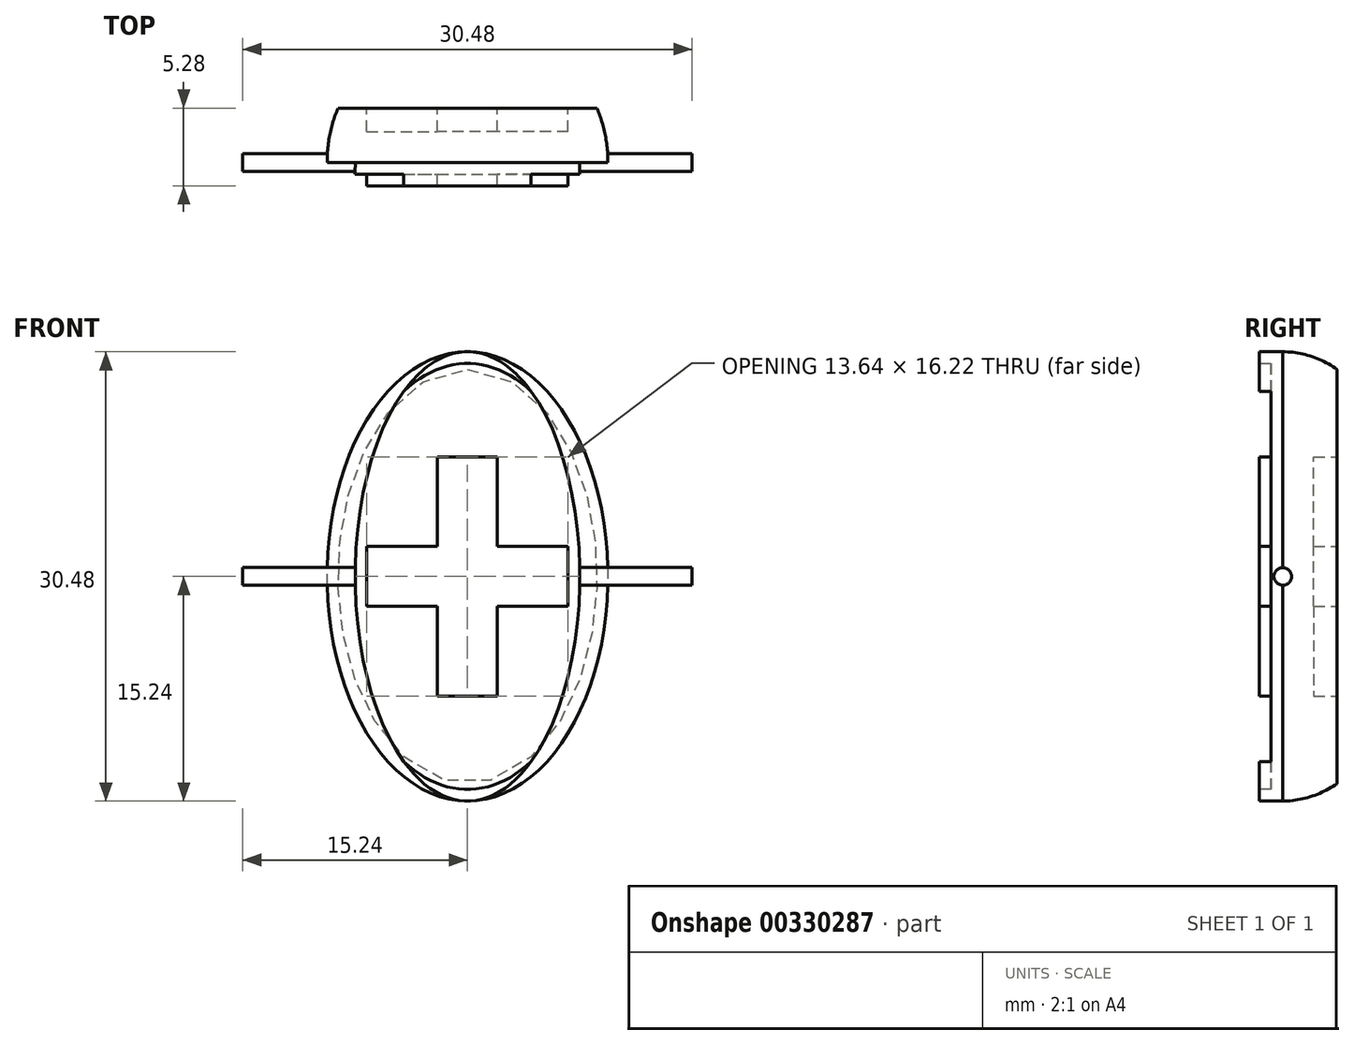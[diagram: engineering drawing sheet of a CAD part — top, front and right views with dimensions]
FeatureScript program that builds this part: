
annotation { "Feature Type Name" : "Feature", "Feature Type Description" : "" }
export const myFeature = defineFeature(function(context is Context, id is Id, definition is map)
    precondition{}
    {
        {
            var Q0;
            Q0=qCreatedBy(makeId("Front.planeOp"),FACE);
            var sketch = newSketch(context, id + "F0", { "sketchPlane" : qUnion([Q0])});
            skEllipticalArc(sketch, "E0", {});
            skLineSegment(sketch, "E1", {"start": v(0, 15.24) * mm, "end": v(0, -15.24) * mm});
            const initialGuessF0  = {"E0": [0, 0, 0, 1, 0.01524, 0.009525, 3.141592653589793, 0]};
            skSetInitialGuess(sketch, initialGuessF0);
            skSolve(sketch);
        }
        {
            var Q0;
            Q0=qSketchRegion(id+"F0",true);
            var Q1;
            Q1=sQuery(id+"F0.wireOp",EDGE,"E1");
            revolve(context, id + "F1", {"entities" : qUnion([Q0]), "axis" : qUnion([Q1]), "revolveType" : RevolveType.ONE_DIRECTION, "oppositeDirection" : true, "angle" : 180 * degree});
        }
        {
            var Q0;
            Q0=qCreatedBy(makeId("Right.planeOp"),FACE);
            var sketch = newSketch(context, id + "F2", { "sketchPlane" : qUnion([Q0])});
            skLineSegment(sketch, "E2.bottom", {"start": v(3.69, 15.9) * mm, "end": v(30.72, 15.9) * mm});
            skLineSegment(sketch, "E2.top", {"start": v(3.69, -22.6) * mm, "end": v(30.72, -22.6) * mm});
            skLineSegment(sketch, "E2.left", {"start": v(3.69, 15.9) * mm, "end": v(3.69, -22.6) * mm});
            skLineSegment(sketch, "E2.right", {"start": v(30.72, 15.9) * mm, "end": v(30.72, -22.6) * mm});
            skSolve(sketch);
        }
        {
            var Q0;
            Q0=qSketchRegion(id+"F2",true);
            extrude(context, id + "F3", {"entities" : qUnion([Q0]), "operationType" : NewBodyOperationType.REMOVE, "oppositeDirection" : true, "depth" : 25.4 * mm, "symmetric" : true});
        }
        {
            var Q0;
            Q0=qCreatedBy(makeId("Right.planeOp"),FACE);
            var sketch = newSketch(context, id + "F4", { "sketchPlane" : qUnion([Q0])});
            skCircle(sketch, "E3", {"center": v(0, 0) * mm, "radius": 0.6 * mm});
            skSolve(sketch);
        }
        {
            var Q0;
            Q0=makeQuery(id+"F1.opRevolve","CAP_FACE",FACE,{"disambiguationData":[OSD([sQuery(id+"F0.wireOp",EDGE,"E0"),sQuery(id+"F0.wireOp",EDGE,"E1")])],"isStart":false});
            var sketch = newSketch(context, id + "F5", { "sketchPlane" : qUnion([Q0])});
            skEllipticalArc(sketch, "E4.0", {});
            skEllipticalArc(sketch, "E4.1", {});
            const initialGuessF5  = {"E4.0": [0, 0, 0, 1, 0.01524, 0.00762, 0, 3.141592653589793], "E4.1": [0, 0, 0, 1, 0.01524, 0.00762, 3.141592653589793, 0]};
            skSetInitialGuess(sketch, initialGuessF5);
            skSolve(sketch);
        }
        {
            var Q0;
            Q0=qSketchRegion(id+"F5",true);
            extrude(context, id + "F6", {"entities" : qUnion([Q0]), "operationType" : NewBodyOperationType.ADD, "depth" : 1.59 * mm});
        }
        {
            var Q0;
            Q0=qSketchRegion(id+"F4",true);
            extrude(context, id + "F7", {"entities" : qUnion([Q0]), "operationType" : NewBodyOperationType.ADD, "depth" : 30.48 * mm, "symmetric" : true});
        }
        {
            var Q0;
            Q0=makeQuery(id+"F6.opExtrude","CAP_FACE",FACE,{"disambiguationData":[OSD([sQuery(id+"F5.wireOp",EDGE,"E4.0"),sQuery(id+"F5.wireOp",EDGE,"E4.1")])],"isStart":false});
            var sketch = newSketch(context, id + "F8", { "sketchPlane" : qUnion([Q0])});
            skEllipse(sketch, "E5", {"center": v(0, 0) * mm, "majorRadius": 14.45 * mm, "minorRadius": 8.73 * mm, "majorAxis": v(0, 1)});
            skSolve(sketch);
        }
        {
            var Q0;
            Q0=qSketchRegion(id+"F8",true);
            extrude(context, id + "F9", {"entities" : qUnion([Q0]), "operationType" : NewBodyOperationType.REMOVE, "oppositeDirection" : true, "depth" : 0.8 * mm});
        }
        {
            var Q0;
            Q0=makeQuery(id+"F9.boolean.opBoolean","COPY",FACE,{"derivedFrom":makeQuery(id+"F9.opExtrude","CAP_FACE",FACE,{"disambiguationData":[OSD([sQuery(id+"F8.wireOp",EDGE,"E5")])],"isStart":false})});
            var sketch = newSketch(context, id + "F10", { "sketchPlane" : qUnion([Q0])});
            skSolve(sketch);
        }
        {
            var Q0;
            Q0=makeQuery(id+"F10.imprint","IMPRINT",FACE,{"disambiguationData":[TD([[makeQuery(id+"F10.imprint","IMPRINT",EDGE,{"derivedFrom":makeQuery(id+"F9.boolean.opBoolean","COPY",EDGE,{"derivedFrom":makeQuery(id+"F9.opExtrude","CAP_EDGE",EDGE,{"disambiguationData":[OSD([sQuery(id+"F8.wireOp",EDGE,"E5")])],"isStart":false})})}),1.0]])]});
            var sketch = newSketch(context, id + "F11", { "sketchPlane" : qUnion([Q0])});
            skLineSegment(sketch, "E6", {"start": v(0, 8.11) * mm, "end": v(-2.03, 8.11) * mm});
            skLineSegment(sketch, "E7", {"start": v(-6.82, 0) * mm, "end": v(-6.82, 2.03) * mm});
            skLineSegment(sketch, "E8", {"start": v(-6.82, 2.03) * mm, "end": v(-2.03, 2.03) * mm});
            skLineSegment(sketch, "E9", {"start": v(-2.03, 2.03) * mm, "end": v(-2.03, 8.11) * mm});
            skLineSegment(sketch, "E10.MirrorCS", {"start": v(-6.82, 0) * mm, "end": v(-6.82, -2.03) * mm});
            skLineSegment(sketch, "E11.MirrorCS", {"start": v(-2.03, -2.03) * mm, "end": v(-2.03, -8.11) * mm});
            skLineSegment(sketch, "E12.MirrorCS", {"start": v(0, -8.11) * mm, "end": v(-2.03, -8.11) * mm});
            skLineSegment(sketch, "E13.MirrorCS", {"start": v(-6.82, -2.03) * mm, "end": v(-2.03, -2.03) * mm});
            skLineSegment(sketch, "E14.MirrorCS", {"start": v(2.03, -2.03) * mm, "end": v(2.03, -8.11) * mm});
            skLineSegment(sketch, "E15.MirrorCS", {"start": v(2.03, 2.03) * mm, "end": v(2.03, 8.11) * mm});
            skLineSegment(sketch, "E16.MirrorCS", {"start": v(6.82, 0) * mm, "end": v(6.82, -2.03) * mm});
            skLineSegment(sketch, "E17.MirrorCS", {"start": v(0, 8.11) * mm, "end": v(2.03, 8.11) * mm});
            skLineSegment(sketch, "E18.MirrorCS", {"start": v(6.82, 0) * mm, "end": v(6.82, 2.03) * mm});
            skLineSegment(sketch, "E19.MirrorCS", {"start": v(6.82, 2.03) * mm, "end": v(2.03, 2.03) * mm});
            skLineSegment(sketch, "E20.MirrorCS", {"start": v(6.82, -2.03) * mm, "end": v(2.03, -2.03) * mm});
            skLineSegment(sketch, "E21.MirrorCS", {"start": v(0, -8.11) * mm, "end": v(2.03, -8.11) * mm});
            skSolve(sketch);
        }
        {
            var Q0;
            Q0=qSketchRegion(id+"F11",true);
            extrude(context, id + "F12", {"entities" : qUnion([Q0]), "operationType" : NewBodyOperationType.ADD, "depth" : 0.8 * mm});
        }
        {
            var Q0;
            Q0=makeQuery(id+"F3.boolean.opBoolean","COPY",FACE,{"derivedFrom":makeQuery(id+"F3.opExtrude","SWEPT_FACE",FACE,{"disambiguationData":[OSD([sQuery(id+"F2.wireOp",EDGE,"E2.left")])]})});
            var sketch = newSketch(context, id + "F13", { "sketchPlane" : qUnion([Q0])});
            skLineSegment(sketch, "E22.0", {"start": v(-2.03, 2.03) * mm, "end": v(-2.03, 8.11) * mm});
            skLineSegment(sketch, "E22.1", {"start": v(0, 8.11) * mm, "end": v(2.03, 8.11) * mm});
            skLineSegment(sketch, "E22.2", {"start": v(0, 8.11) * mm, "end": v(-2.03, 8.11) * mm});
            skLineSegment(sketch, "E22.3", {"start": v(2.03, 2.03) * mm, "end": v(2.03, 8.11) * mm});
            skLineSegment(sketch, "E22.4", {"start": v(6.82, 2.03) * mm, "end": v(2.03, 2.03) * mm});
            skLineSegment(sketch, "E22.5", {"start": v(6.82, 0) * mm, "end": v(6.82, 2.03) * mm});
            skLineSegment(sketch, "E22.6", {"start": v(6.82, 0) * mm, "end": v(6.82, -2.03) * mm});
            skLineSegment(sketch, "E22.7", {"start": v(6.82, -2.03) * mm, "end": v(2.03, -2.03) * mm});
            skLineSegment(sketch, "E22.8", {"start": v(2.03, -2.03) * mm, "end": v(2.03, -8.11) * mm});
            skLineSegment(sketch, "E22.9", {"start": v(0, -8.11) * mm, "end": v(2.03, -8.11) * mm});
            skLineSegment(sketch, "E22.10", {"start": v(0, -8.11) * mm, "end": v(-2.03, -8.11) * mm});
            skLineSegment(sketch, "E22.11", {"start": v(-2.03, -2.03) * mm, "end": v(-2.03, -8.11) * mm});
            skLineSegment(sketch, "E22.12", {"start": v(-6.82, -2.03) * mm, "end": v(-2.03, -2.03) * mm});
            skLineSegment(sketch, "E22.13", {"start": v(-6.82, 0) * mm, "end": v(-6.82, -2.03) * mm});
            skLineSegment(sketch, "E22.14", {"start": v(-6.82, 0) * mm, "end": v(-6.82, 2.03) * mm});
            skLineSegment(sketch, "E22.15", {"start": v(-6.82, 2.03) * mm, "end": v(-2.03, 2.03) * mm});
            skSolve(sketch);
        }
        {
            var Q0;
            Q0=qSketchRegion(id+"F13",true);
            extrude(context, id + "F14", {"entities" : qUnion([Q0]), "operationType" : NewBodyOperationType.REMOVE, "oppositeDirection" : true, "depth" : 1.59 * mm});
        }
    });
